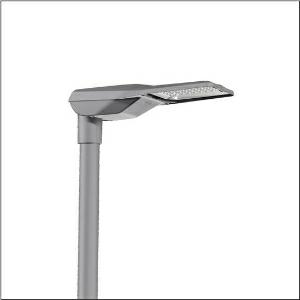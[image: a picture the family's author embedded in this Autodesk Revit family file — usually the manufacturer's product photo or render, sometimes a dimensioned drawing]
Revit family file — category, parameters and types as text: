
# Revit family: streetlight_sl_21_iq_mini___p0_8ab_5xe2r31d08gb_0de2
name_source: partatom
category: Lighting Fixtures
units: mm (PartAtom-declared; Revit-internal decimal feet)

## family parameters
Cut with Voids When Loaded = No
Host = Face
Light Source = No
Part Type = Normal
Room Calculation Point = No
Round Connector Dimension = Use Diameter
Shared = No

## types (1)
- --- (1 x LED, 4930 lm, 37.1 W, 3000K)
    Apparent Load = 37 VA
    CIE Flux Codes = 36 71 98 100 100
    Color Rendering = 70
    Color Temperature = 3000K
    Default Elevation = 1800 mm
    Description = Streetlight SL 21 iQ mini, mast luminaire, primary light control with lens, of PMMA, primary optical cover: cover, of toughened safety glass, transparent, light distribution: P0.8aB, light emission: direct distribution, primary light characteristic: asymmetric, installation type: post-top, side-entry, LED, High Power LED, rated luminous flux: 4.930lm, luminous efficacy: 133lm/W, light colour: 730, colour temperature: 3000K, control gear: iQ-Comfort, control: pre-setting: linear dimming characteristic, Auto-Match, Temp-Guard, Lumen-Switch, Night-Set, Smart-Wire, Light-Fading, Desk-Remote (wireless, voltage-free reading and setting of iQ features in the workshop via application-optimized NFC function/RFID function), optimised constant luminous flux control (CLO 2.0), mains connection: 220..240V, AC, 50/60Hz, start of lifetime: 37W, end of service life: 39W, reduction: 18W, luminaire housing, of diecast aluminium, powder-coated, SITECO metallic grey (DB 702S), corrosivity category C5 high according to DIN EN ISO 12944, please order mast flange separately, inclination adjustable: 0°, 5°, 10°, 15°, sealing non-destructively replaceable, multi-level sealing system, length: 628mm, width: 235mm, height: 110mm, mast flange for spigot size: 42mm (side-entry): 5XC10008XM4, 60/48mm (side-entry/post-top): 5XC10108XM2, 76/60mm (side-entry/post-top): 5XC10108XM1, mounting height: 4..8m, protection rating (complete): IP66, insulation class (complete): insulation class II (safety insulation), certification: CE, ENEC, ENEC+, VDE, impact resistance: IK10, permissible operating ambient temperature for outdoor applications: -40..+50°C, standard-compliant lighting for roads and squares, packaging unit: 1 piece

Light Distribution: P0.8aB
    Height = 110 mm
    Lamp = 1 x LED
    Lamp Light Flux = 4930 lm
    Lamp Power = 37.1 W
    Lamp count = 1
    Length = 625 mm
    Luminous efficacy = 133 lm/W
    Manufacturer = Siteco
    ModVariant = No
    Model = 5XE2R31D08GB
    Number of Poles = 1
    OnlyDefault = Yes
    Power Factor = 1
    Product Name = Streetlight SL 21 iQ mini | P0.8aB
    Product group = mast luminaire | pylon top
    ProductGroupID = 6100
    Protection Class = Protection class II
    Protection Degree = IP 66
    RLX_Detail_Level = 1
    RLX_Emergency_Light_Flux = 0 lm
    RLX_Emergency_Type = 0
    RLX_Emergency_Type_DB = No
    RlxData = <blob elided: 93885 chars, md5=ad52c22d>
    Socket = socket
    Standby Power = 0 W
    System Light Flux = 4930 lm
    System Power = 37 W
    Type Comments = factory setting: luminous flux: 100 % | dim-lin: 254 | 385 mA
    Type Image = l_1003519.jpg
    URL = http://relux.com
    VarID = @adj_082301
    Voltage = 0 V
    Weight = 0.00 kg
    Width = 234 mm

## geometry (parser evidence)
native form markers: Blend x4, Sweep x11
no freeform markers — native parametric forms only
